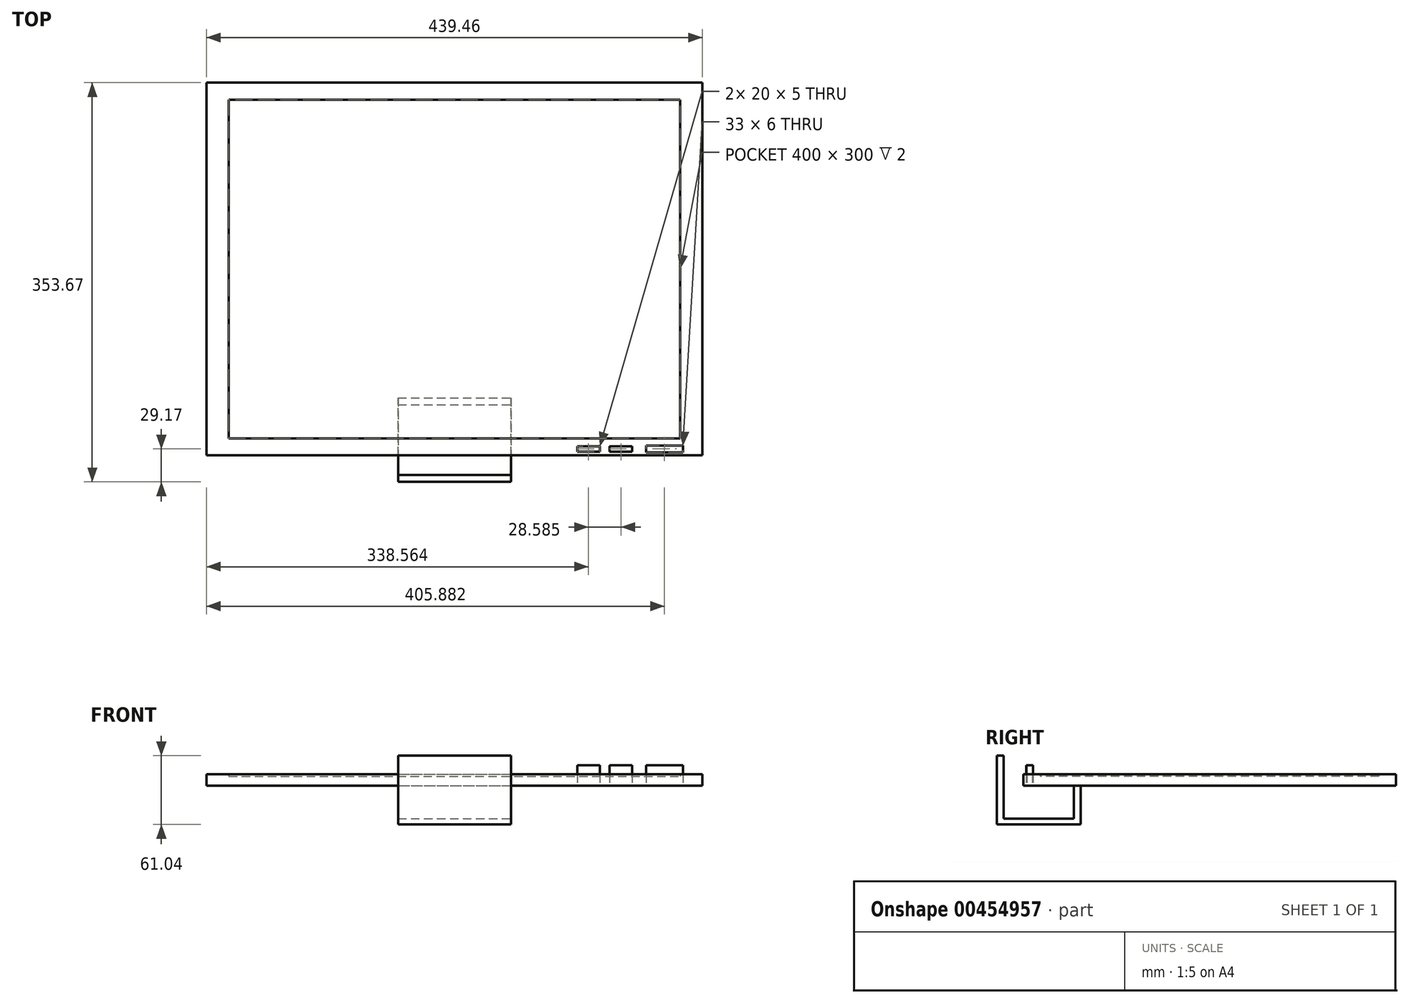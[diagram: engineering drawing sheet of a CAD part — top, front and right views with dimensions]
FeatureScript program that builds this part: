
annotation { "Feature Type Name" : "Feature", "Feature Type Description" : "" }
export const myFeature = defineFeature(function(context is Context, id is Id, definition is map)
    precondition{}
    {
        {
            var Q0;
            Q0=qCreatedBy(makeId("Top.planeOp"),FACE);
            var sketch = newSketch(context, id + "F0", { "sketchPlane" : qUnion([Q0])});
            skLineSegment(sketch, "E0.bottom", {"start": v(-200, 150) * mm, "end": v(200, 150) * mm});
            skLineSegment(sketch, "E0.top", {"start": v(-200, -150) * mm, "end": v(200, -150) * mm});
            skLineSegment(sketch, "E0.left", {"start": v(-200, 150) * mm, "end": v(-200, -150) * mm});
            skLineSegment(sketch, "E0.right", {"start": v(200, 150) * mm, "end": v(200, -150) * mm});
            skPoint(sketch, "E0.middle", {"position": v(0, 0) * mm});
            skLineSegment(sketch, "E1.bottom", {"start": v(-219.73, 165) * mm, "end": v(219.73, 165) * mm});
            skLineSegment(sketch, "E1.top", {"start": v(-219.73, -165) * mm, "end": v(219.73, -165) * mm});
            skLineSegment(sketch, "E1.left", {"start": v(-219.73, 165) * mm, "end": v(-219.73, -165) * mm});
            skLineSegment(sketch, "E1.right", {"start": v(219.73, 165) * mm, "end": v(219.73, -165) * mm});
            skLineSegment(sketch, "E2.bottom", {"start": v(169.65, -156.5) * mm, "end": v(202.65, -156.5) * mm});
            skLineSegment(sketch, "E2.top", {"start": v(169.65, -162.5) * mm, "end": v(202.65, -162.5) * mm});
            skLineSegment(sketch, "E2.left", {"start": v(169.65, -156.5) * mm, "end": v(169.65, -162.5) * mm});
            skLineSegment(sketch, "E2.right", {"start": v(202.65, -156.5) * mm, "end": v(202.65, -162.5) * mm});
            skPoint(sketch, "E2.middle", {"position": v(186.15, -159.5) * mm});
            skLineSegment(sketch, "E3.bottom", {"start": v(137.42, -157) * mm, "end": v(157.42, -157) * mm});
            skLineSegment(sketch, "E3.top", {"start": v(137.42, -162) * mm, "end": v(157.42, -162) * mm});
            skLineSegment(sketch, "E3.left", {"start": v(137.42, -157) * mm, "end": v(137.42, -162) * mm});
            skLineSegment(sketch, "E3.right", {"start": v(157.42, -157) * mm, "end": v(157.42, -162) * mm});
            skPoint(sketch, "E3.middle", {"position": v(147.42, -159.5) * mm});
            skPoint(sketch, "E3.middle.positionSnap0", {"position": v(169.65, -159.5) * mm});
            skPoint(sketch, "E3.centerSnap0", {"position": v(169.65, -159.5) * mm});
            skLineSegment(sketch, "E4.bottom", {"start": v(108.83, -157) * mm, "end": v(128.83, -157) * mm});
            skLineSegment(sketch, "E4.top", {"start": v(108.83, -162) * mm, "end": v(128.83, -162) * mm});
            skLineSegment(sketch, "E4.left", {"start": v(108.83, -157) * mm, "end": v(108.83, -162) * mm});
            skLineSegment(sketch, "E4.right", {"start": v(128.83, -157) * mm, "end": v(128.83, -162) * mm});
            skPoint(sketch, "E4.middle", {"position": v(118.83, -159.5) * mm});
            skPoint(sketch, "E4.middle.positionSnap0", {"position": v(137.42, -159.5) * mm});
            skPoint(sketch, "E4.centerSnap0", {"position": v(137.42, -159.5) * mm});
            skSolve(sketch);
        }
        {
            var Q0;
            Q0=makeQuery(id+"F0.imprint","IMPRINT",FACE,{"disambiguationData":[TD([[makeQuery(id+"F0.imprint","IMPRINT",EDGE,{"derivedFrom":sQuery(id+"F0.wireOp",EDGE,"E0.bottom")}),1.0]])]});
            var Q1;
            Q1=sQuery(id+"F0.wireOp",EDGE,"E2.bottom");
            var Q2;
            Q2=sQuery(id+"F0.wireOp",EDGE,"E2.left");
            var Q3;
            Q3=sQuery(id+"F0.wireOp",EDGE,"E2.right");
            var Q4;
            Q4=sQuery(id+"F0.wireOp",EDGE,"E2.top");
            extrude(context, id + "F1", {"entities" : qUnion([Q0]), "surfaceEntities" : qUnion([Q1, Q2, Q3, Q4]), "depth" : 10 * mm});
        }
        {
            var Q0;
            Q0=qCreatedBy(makeId("Top.planeOp"),FACE);
            var sketch = newSketch(context, id + "F2", { "sketchPlane" : qUnion([Q0])});
            skLineSegment(sketch, "E5.bottom", {"start": v(-201.94, 150.47) * mm, "end": v(200.06, 150.47) * mm});
            skLineSegment(sketch, "E5.top", {"start": v(-201.94, -151.53) * mm, "end": v(200.06, -151.53) * mm});
            skLineSegment(sketch, "E5.left", {"start": v(-201.94, 150.47) * mm, "end": v(-201.94, -151.53) * mm});
            skLineSegment(sketch, "E5.right", {"start": v(200.06, 150.47) * mm, "end": v(200.06, -151.53) * mm});
            skSolve(sketch);
        }
        {
            var Q0;
            Q0 = qSketchRegion(id + "F2", true);
            extrude(context, id + "F3", {"entities" : qUnion([Q0]), "operationType" : NewBodyOperationType.ADD, "depth" : 8 * mm});
        }
        {
            var Q0;
            Q0=qCreatedBy(makeId("Right.planeOp"),FACE);
            var sketch = newSketch(context, id + "F4", { "sketchPlane" : qUnion([Q0])});
            skLineSegment(sketch, "E6", {"start": v(-114.3, 0) * mm, "end": v(-114.3, -34.52) * mm});
            skLineSegment(sketch, "E7", {"start": v(-114.3, -34.52) * mm, "end": v(-188.67, -34.52) * mm});
            skLineSegment(sketch, "E8", {"start": v(-188.67, -34.52) * mm, "end": v(-188.67, 26.52) * mm});
            skLineSegment(sketch, "E9", {"start": v(-188.67, 26.52) * mm, "end": v(-182.56, 26.52) * mm});
            skLineSegment(sketch, "E10", {"start": v(-182.56, 26.52) * mm, "end": v(-182.56, -29.33) * mm});
            skLineSegment(sketch, "E11", {"start": v(-182.56, -29.33) * mm, "end": v(-120.32, -29.33) * mm});
            skLineSegment(sketch, "E12", {"start": v(-120.32, -29.33) * mm, "end": v(-120.32, 0) * mm});
            skLineSegment(sketch, "E13", {"start": v(-120.32, 0) * mm, "end": v(-114.3, 0) * mm});
            skSolve(sketch);
        }
        {
            var Q0;
            Q0=makeQuery(id+"F4.imprint","IMPRINT",FACE,{"disambiguationData":[TD([[makeQuery(id+"F4.imprint","IMPRINT",EDGE,{"derivedFrom":sQuery(id+"F4.wireOp",EDGE,"E6")}),-1.0]])]});
            extrude(context, id + "F5", {"entities" : qUnion([Q0]), "operationType" : NewBodyOperationType.ADD, "endBound" : BoundingType.SYMMETRIC, "oppositeDirection" : true, "depth" : 100 * mm});
        }
        {
            var Q0;
            Q0=makeQuery(id+"F1.opExtrude","CAP_FACE",FACE,{"disambiguationData":[OSD([sQuery(id+"F0.wireOp",EDGE,"E0.bottom"),sQuery(id+"F0.wireOp",EDGE,"E0.top"),sQuery(id+"F0.wireOp",EDGE,"E0.left"),sQuery(id+"F0.wireOp",EDGE,"E0.right"),sQuery(id+"F0.wireOp",EDGE,"E1.bottom"),sQuery(id+"F0.wireOp",EDGE,"E1.top"),sQuery(id+"F0.wireOp",EDGE,"E1.left"),sQuery(id+"F0.wireOp",EDGE,"E1.right"),sQuery(id+"F0.wireOp",EDGE,"E2.bottom"),sQuery(id+"F0.wireOp",EDGE,"E2.top"),sQuery(id+"F0.wireOp",EDGE,"E2.left"),sQuery(id+"F0.wireOp",EDGE,"E2.right"),sQuery(id+"F0.wireOp",EDGE,"E3.bottom"),sQuery(id+"F0.wireOp",EDGE,"E3.top"),sQuery(id+"F0.wireOp",EDGE,"E3.left"),sQuery(id+"F0.wireOp",EDGE,"E3.right"),sQuery(id+"F0.wireOp",EDGE,"E4.bottom"),sQuery(id+"F0.wireOp",EDGE,"E4.top"),sQuery(id+"F0.wireOp",EDGE,"E4.left"),sQuery(id+"F0.wireOp",EDGE,"E4.right")])],"isStart":false});
            var sketch = newSketch(context, id + "F6", { "sketchPlane" : qUnion([Q0])});
            skLineSegment(sketch, "E14.bottom", {"start": v(169.65, -156.5) * mm, "end": v(202.65, -156.5) * mm});
            skLineSegment(sketch, "E14.top", {"start": v(169.65, -162.5) * mm, "end": v(202.65, -162.5) * mm});
            skLineSegment(sketch, "E14.left", {"start": v(169.65, -156.5) * mm, "end": v(169.65, -162.5) * mm});
            skLineSegment(sketch, "E14.right", {"start": v(202.65, -156.5) * mm, "end": v(202.65, -162.5) * mm});
            skLineSegment(sketch, "E15.bottom", {"start": v(137.42, -157) * mm, "end": v(157.42, -157) * mm});
            skLineSegment(sketch, "E15.top", {"start": v(137.42, -162) * mm, "end": v(157.42, -162) * mm});
            skLineSegment(sketch, "E15.left", {"start": v(137.42, -157) * mm, "end": v(137.42, -162) * mm});
            skLineSegment(sketch, "E15.right", {"start": v(157.42, -157) * mm, "end": v(157.42, -162) * mm});
            skLineSegment(sketch, "E16.bottom", {"start": v(108.83, -157) * mm, "end": v(128.83, -157) * mm});
            skLineSegment(sketch, "E16.top", {"start": v(108.83, -162) * mm, "end": v(128.83, -162) * mm});
            skLineSegment(sketch, "E16.left", {"start": v(108.83, -157) * mm, "end": v(108.83, -162) * mm});
            skLineSegment(sketch, "E16.right", {"start": v(128.83, -157) * mm, "end": v(128.83, -162) * mm});
            skSolve(sketch);
        }
        {
            var Q0;
            Q0 = qSketchRegion(id + "F6", true);
            extrude(context, id + "F7", {"entities" : qUnion([Q0]), "depth" : 8 * mm});
        }
    });
